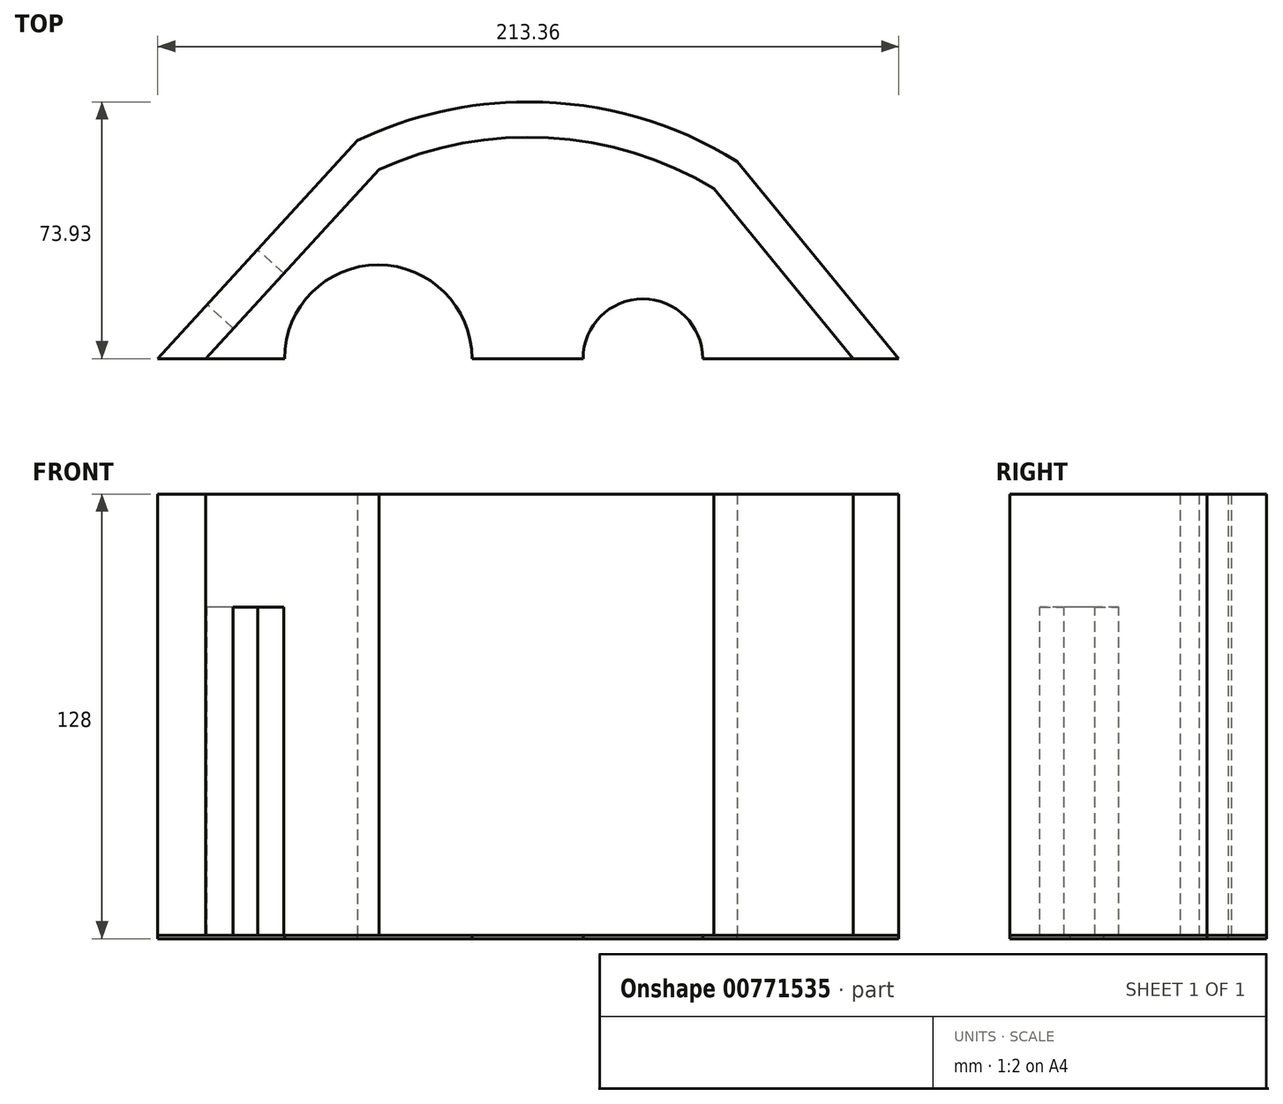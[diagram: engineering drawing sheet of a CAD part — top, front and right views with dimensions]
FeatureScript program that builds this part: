
annotation { "Feature Type Name" : "Feature", "Feature Type Description" : "" }
export const myFeature = defineFeature(function(context is Context, id is Id, definition is map)
    precondition{}
    {
        {
            var Q0;
            Q0=qCreatedBy(makeId("Top.planeOp"),FACE);
            var sketch = newSketch(context, id + "F0", { "sketchPlane" : qUnion([Q0])});
            skLineSegment(sketch, "E0", {"start": v(-47.84, 26.82) * mm, "end": v(37.98, 120.44) * mm});
            skLineSegment(sketch, "E1", {"start": v(37.98, 120.44) * mm, "end": v(88.78, 120.44) * mm});
            skLineSegment(sketch, "E2", {"start": v(-47.84, 26.82) * mm, "end": v(-4.14, 26.82) * mm});
            skLineSegment(sketch, "E3", {"start": v(165.52, 26.82) * mm, "end": v(88.78, 120.44) * mm});
            skLineSegment(sketch, "E4", {"start": v(165.52, 26.82) * mm, "end": v(109.06, 26.82) * mm});
            skCircle(sketch, "E5", {"center": v(15.66, 26.82) * mm, "radius": 12.7 * mm});
            skCircle(sketch, "E6", {"center": v(91.86, 26.82) * mm, "radius": 12.7 * mm});
            skLineSegment(sketch, "E7", {"start": v(154.48, 40.3) * mm, "end": v(122.28, 79.58) * mm});
            skArc(sketch, "E8", {"start": v(109.06, 26.82) * mm, "mid": v(91.86, 44.02) * mm, "end": v(74.66, 26.82) * mm});
            skArc(sketch, "E9", {"start": v(35.46, 26.82) * mm, "mid": v(15.66, 46.62) * mm, "end": v(-4.14, 26.82) * mm});
            skLineSegment(sketch, "E10.trimOffspring", {"start": v(35.46, 26.82) * mm, "end": v(74.66, 26.82) * mm});
            skLineSegment(sketch, "E11.trimOffspring", {"start": v(109.06, 26.82) * mm, "end": v(165.52, 26.82) * mm});
            skSolve(sketch);
        }
        {
            var Q0;
            Q0 = qSketchRegion(id + "F0", true);
            extrude(context, id + "F1", {"entities" : qUnion([Q0]), "depth" : 1 * mm, "offsetDistance" : 25.4 * mm});
        }
        {
            var Q0;
            Q0=makeQuery(id+"F1.opExtrude","SWEPT_BODY",BODY,{"disambiguationData":[OSD([sQuery(id+"F0.wireOp",EDGE,"E6")])]});
            deleteBodies(context, id + "F2", {"entities" : qUnion([Q0])});
        }
        {
            var Q0;
            Q0=makeQuery(id+"F1.opExtrude","SWEPT_BODY",BODY,{"disambiguationData":[OSD([sQuery(id+"F0.wireOp",EDGE,"E5")])]});
            deleteBodies(context, id + "F3", {"entities" : qUnion([Q0])});
        }
        {
            var Q0;
            Q0=makeQuery(id+"F1.opExtrude","CAP_FACE",FACE,{"disambiguationData":[OSD([sQuery(id+"F0.wireOp",EDGE,"E0"),sQuery(id+"F0.wireOp",EDGE,"E1"),sQuery(id+"F0.wireOp",EDGE,"E3"),sQuery(id+"F0.wireOp",EDGE,"E2"),sQuery(id+"F0.wireOp",EDGE,"E7"),sQuery(id+"F0.wireOp",EDGE,"E8"),sQuery(id+"F0.wireOp",EDGE,"E9"),sQuery(id+"F0.wireOp",EDGE,"E10.trimOffspring"),sQuery(id+"F0.wireOp",EDGE,"E11.trimOffspring")])],"isStart":false});
            var sketch = newSketch(context, id + "F4", { "sketchPlane" : qUnion([Q0])});
            skLineSegment(sketch, "E12", {"start": v(-32.88, 96.1) * mm, "end": v(188.48, 96.1) * mm});
            skLineSegment(sketch, "E13", {"start": v(188.48, 96.1) * mm, "end": v(188.48, 149.6) * mm});
            skLineSegment(sketch, "E14", {"start": v(188.48, 149.6) * mm, "end": v(-32.88, 149.6) * mm});
            skLineSegment(sketch, "E15", {"start": v(-32.88, 96.1) * mm, "end": v(-32.88, 149.6) * mm});
            skSolve(sketch);
        }
        {
            var Q0;
            {var subQ4=sQuery(id+"F4.wireOp",EDGE,"E13");Q0=makeQuery(id+"F4.imprint","IMPRINT",FACE,{"disambiguationData":[TD([[makeQuery(id+"F4.imprint","IMPRINT",EDGE,{"derivedFrom":subQ4}),1.0]])]});}
            extrude(context, id + "F5", {"entities" : qUnion([Q0]), "operationType" : NewBodyOperationType.REMOVE, "oppositeDirection" : true, "depth" : 25.4 * mm, "offsetDistance" : 25.4 * mm});
        }
        {
            var Q0;
            Q0=makeQuery(id+"F1.opExtrude","CAP_FACE",FACE,{"disambiguationData":[OSD([sQuery(id+"F0.wireOp",EDGE,"E0"),sQuery(id+"F0.wireOp",EDGE,"E1"),sQuery(id+"F0.wireOp",EDGE,"E3"),sQuery(id+"F0.wireOp",EDGE,"E2"),sQuery(id+"F0.wireOp",EDGE,"E7"),sQuery(id+"F0.wireOp",EDGE,"E8"),sQuery(id+"F0.wireOp",EDGE,"E9"),sQuery(id+"F0.wireOp",EDGE,"E10.trimOffspring"),sQuery(id+"F0.wireOp",EDGE,"E11.trimOffspring")])],"isStart":false});
            var sketch = newSketch(context, id + "F6", { "sketchPlane" : qUnion([Q0])});
            skLineSegment(sketch, "E16", {"start": v(-24.14, 100.75) * mm, "end": v(192.58, 100.75) * mm});
            skLineSegment(sketch, "E17", {"start": v(192.58, 100.75) * mm, "end": v(184.87, 143.2) * mm});
            skLineSegment(sketch, "E18", {"start": v(184.87, 143.2) * mm, "end": v(-26.68, 149.4) * mm});
            skLineSegment(sketch, "E19", {"start": v(-26.68, 149.4) * mm, "end": v(-24.14, 100.75) * mm});
            skSolve(sketch);
        }
        {
            var Q0;
            Q0 = qSketchRegion(id + "F6", true);
            extrude(context, id + "F7", {"entities" : qUnion([Q0]), "operationType" : NewBodyOperationType.REMOVE, "oppositeDirection" : true, "depth" : 25.4 * mm, "offsetDistance" : 25.4 * mm});
        }
        {
            var Q0;
            Q0=makeQuery(id+"F1.opExtrude","CAP_FACE",FACE,{"disambiguationData":[OSD([sQuery(id+"F0.wireOp",EDGE,"E0"),sQuery(id+"F0.wireOp",EDGE,"E1"),sQuery(id+"F0.wireOp",EDGE,"E3"),sQuery(id+"F0.wireOp",EDGE,"E2"),sQuery(id+"F0.wireOp",EDGE,"E7"),sQuery(id+"F0.wireOp",EDGE,"E8"),sQuery(id+"F0.wireOp",EDGE,"E9"),sQuery(id+"F0.wireOp",EDGE,"E10.trimOffspring"),sQuery(id+"F0.wireOp",EDGE,"E11.trimOffspring")])],"isStart":false});
            var sketch = newSketch(context, id + "F8", { "sketchPlane" : qUnion([Q0])});
            skCircle(sketch, "E20", {"center": v(58.84, -13.19) * mm, "radius": 113.94 * mm});
            skPoint(sketch, "E20.first.point", {"position": v(-47.84, 26.82) * mm});
            skPoint(sketch, "E20.second.point", {"position": v(165.52, 26.82) * mm});
            skPoint(sketch, "E20.third.point", {"position": v(58.65, 100.75) * mm});
            skSolve(sketch);
        }
        {
            var Q0;
            {var subQ0=makeQuery(id+"F1.opExtrude","CAP_EDGE",EDGE,{"disambiguationData":[OSD([sQuery(id+"F0.wireOp",EDGE,"E2")])],"isStart":false});Q0=makeQuery(id+"F8.imprint","IMPRINT",FACE,{"disambiguationData":[TD([[makeQuery(id+"F8.imprint","IMPRINT",EDGE,{"derivedFrom":subQ0}),-1.0]])]});}
            var Q1;
            {var subQ0=sQuery(id+"F8.wireOp",EDGE,"E20");var subQ1=makeQuery(id+"F1.opExtrude","CAP_EDGE",EDGE,{"disambiguationData":[OSD([sQuery(id+"F0.wireOp",EDGE,"E3"),sQuery(id+"F0.wireOp",EDGE,"E7")])],"isStart":false});var subQ3=makeQuery(id+"F8.imprint","INTERSECT",VERTEX,{"derivedFrom":[subQ1,subQ0]});Q1=makeQuery(id+"F8.imprint","IMPRINT",FACE,{"disambiguationData":[TD([[makeQuery(id+"F8.imprint","IMPRINT",EDGE,{"disambiguationData":[TD([[subQ3,1.0]])],"derivedFrom":subQ0}),1.0]])]});}
            var Q2;
            {var subQ0=sQuery(id+"F8.wireOp",EDGE,"E20");var subQ1=makeQuery(id+"F7.boolean.opBoolean","COPY",EDGE,{"derivedFrom":makeQuery(id+"F7.opExtrude","CAP_EDGE",EDGE,{"disambiguationData":[OSD([sQuery(id+"F6.wireOp",EDGE,"E16")])],"isStart":true})});var subQ2=makeQuery(id+"F8.imprint","INTERSECT",VERTEX,{"disambiguationData":[OD(0.0)],"derivedFrom":[subQ1,subQ0]});Q2=makeQuery(id+"F8.imprint","IMPRINT",FACE,{"disambiguationData":[TD([[makeQuery(id+"F8.imprint","IMPRINT",EDGE,{"disambiguationData":[TD([[subQ2,-1.0]])],"derivedFrom":subQ0}),1.0]])]});}
            var Q3;
            {var subQ0=sQuery(id+"F8.wireOp",EDGE,"E20");var subQ1=makeQuery(id+"F1.opExtrude","CAP_EDGE",EDGE,{"disambiguationData":[OSD([sQuery(id+"F0.wireOp",EDGE,"E0")])],"isStart":false});var subQ3=makeQuery(id+"F8.imprint","INTERSECT",VERTEX,{"derivedFrom":[subQ1,subQ0]});Q3=makeQuery(id+"F8.imprint","IMPRINT",FACE,{"disambiguationData":[TD([[makeQuery(id+"F8.imprint","IMPRINT",EDGE,{"disambiguationData":[TD([[subQ3,-1.0]])],"derivedFrom":subQ0}),1.0]])]});}
            var Q4;
            {var subQ0=sQuery(id+"F8.wireOp",EDGE,"E20");var subQ1=makeQuery(id+"F7.boolean.opBoolean","COPY",EDGE,{"derivedFrom":makeQuery(id+"F7.opExtrude","CAP_EDGE",EDGE,{"disambiguationData":[OSD([sQuery(id+"F6.wireOp",EDGE,"E16")])],"isStart":true})});var subQ2=makeQuery(id+"F8.imprint","INTERSECT",VERTEX,{"disambiguationData":[OD(1.0)],"derivedFrom":[subQ1,subQ0]});Q4=makeQuery(id+"F8.imprint","IMPRINT",FACE,{"disambiguationData":[TD([[makeQuery(id+"F8.imprint","IMPRINT",EDGE,{"disambiguationData":[TD([[subQ2,-1.0]])],"derivedFrom":subQ0}),-1.0]])]});}
            var Q5;
            {var subQ0=sQuery(id+"F8.wireOp",EDGE,"E20");var subQ3=makeQuery(id+"F7.boolean.opBoolean","COPY",EDGE,{"derivedFrom":makeQuery(id+"F7.opExtrude","CAP_EDGE",EDGE,{"disambiguationData":[OSD([sQuery(id+"F6.wireOp",EDGE,"E16")])],"isStart":true})});var subQ4=makeQuery(id+"F8.imprint","INTERSECT",VERTEX,{"disambiguationData":[OD(0.0)],"derivedFrom":[subQ3,subQ0]});Q5=makeQuery(id+"F8.imprint","IMPRINT",FACE,{"disambiguationData":[TD([[makeQuery(id+"F8.imprint","IMPRINT",EDGE,{"disambiguationData":[TD([[subQ4,1.0]])],"derivedFrom":subQ0}),-1.0]])]});}
            extrude(context, id + "F9", {"entities" : qUnion([Q0, Q1, Q2, Q3, Q4, Q5]), "operationType" : NewBodyOperationType.REMOVE, "oppositeDirection" : true, "depth" : 25.4 * mm, "offsetDistance" : 25.4 * mm});
        }
        {
            var Q0;
            Q0=makeQuery(id+"F1.opExtrude","CAP_FACE",FACE,{"disambiguationData":[OSD([sQuery(id+"F0.wireOp",EDGE,"E0"),sQuery(id+"F0.wireOp",EDGE,"E1"),sQuery(id+"F0.wireOp",EDGE,"E3"),sQuery(id+"F0.wireOp",EDGE,"E2"),sQuery(id+"F0.wireOp",EDGE,"E7"),sQuery(id+"F0.wireOp",EDGE,"E8"),sQuery(id+"F0.wireOp",EDGE,"E9"),sQuery(id+"F0.wireOp",EDGE,"E10.trimOffspring"),sQuery(id+"F0.wireOp",EDGE,"E11.trimOffspring")])],"isStart":false});
            var sketch = newSketch(context, id + "F10", { "sketchPlane" : qUnion([Q0])});
            skCircle(sketch, "E21", {"center": v(15.66, 26.82) * mm, "radius": 27 * mm});
            skSolve(sketch);
        }
        {
            var Q0;
            {var subQ5=makeQuery(id+"F1.opExtrude","CAP_EDGE",EDGE,{"disambiguationData":[OSD([sQuery(id+"F0.wireOp",EDGE,"E9")])],"isStart":false});Q0=makeQuery(id+"F10.imprint","IMPRINT",FACE,{"disambiguationData":[TD([[makeQuery(id+"F10.imprint","IMPRINT",EDGE,{"derivedFrom":subQ5}),-1.0]])]});}
            extrude(context, id + "F11", {"entities" : qUnion([Q0]), "operationType" : NewBodyOperationType.REMOVE, "oppositeDirection" : true, "depth" : 25.4 * mm, "offsetDistance" : 25.4 * mm});
        }
        {
            var Q0;
            Q0=makeQuery(id+"F1.opExtrude","CAP_FACE",FACE,{"disambiguationData":[OSD([sQuery(id+"F0.wireOp",EDGE,"E0"),sQuery(id+"F0.wireOp",EDGE,"E1"),sQuery(id+"F0.wireOp",EDGE,"E3"),sQuery(id+"F0.wireOp",EDGE,"E2"),sQuery(id+"F0.wireOp",EDGE,"E7"),sQuery(id+"F0.wireOp",EDGE,"E8"),sQuery(id+"F0.wireOp",EDGE,"E9"),sQuery(id+"F0.wireOp",EDGE,"E10.trimOffspring"),sQuery(id+"F0.wireOp",EDGE,"E11.trimOffspring")])],"isStart":false});
            var sketch = newSketch(context, id + "F12", { "sketchPlane" : qUnion([Q0])});
            skArc(sketch, "E22", {"start": v(119, 83.57) * mm, "mid": v(65.14, 100.58) * mm, "end": v(9.72, 89.62) * mm});
            skPoint(sketch, "E22.first.point", {"position": v(9.72, 89.62) * mm});
            skPoint(sketch, "E22.second.point", {"position": v(119, 83.57) * mm});
            skPoint(sketch, "E22.third.point", {"position": v(58.65, 100.75) * mm});
            skLineSegment(sketch, "E23", {"start": v(-47.84, 26.82) * mm, "end": v(9.72, 89.62) * mm});
            skLineSegment(sketch, "E24", {"start": v(165.52, 26.82) * mm, "end": v(119, 83.57) * mm});
            skLineSegment(sketch, "E25.0", {"start": v(-34.06, 26.82) * mm, "end": v(15.85, 81.27) * mm});
            skArc(sketch, "E25.1", {"start": v(112.23, 75.8) * mm, "mid": v(64.72, 90.42) * mm, "end": v(15.85, 81.27) * mm});
            skLineSegment(sketch, "E25.2", {"start": v(152.38, 26.82) * mm, "end": v(112.23, 75.8) * mm});
            skLineSegment(sketch, "E26", {"start": v(-47.84, 26.82) * mm, "end": v(-34.06, 26.82) * mm});
            skLineSegment(sketch, "E27", {"start": v(165.52, 26.82) * mm, "end": v(152.38, 26.82) * mm});
            skPoint(sketch, "E28.orphan", {"position": v(-29.59, 26.82) * mm});
            skSolve(sketch);
        }
        {
            var Q0;
            {var subQ1=sQuery(id+"F12.wireOp",EDGE,"E23");Q0=makeQuery(id+"F12.imprint","IMPRINT",FACE,{"disambiguationData":[TD([[makeQuery(id+"F12.imprint","IMPRINT",EDGE,{"derivedFrom":subQ1}),-1.0]])]});}
            extrude(context, id + "F13", {"entities" : qUnion([Q0]), "depth" : 127 * mm, "offsetDistance" : 25.4 * mm});
        }
        {
            var Q0;
            Q0=makeQuery(id+"F13.opExtrude","SWEPT_FACE",FACE,{"disambiguationData":[OSD([sQuery(id+"F12.wireOp",EDGE,"E23")])]});
            var sketch = newSketch(context, id + "F14", { "sketchPlane" : qUnion([Q0])});
            skLineSegment(sketch, "E29.bottom", {"start": v(-30.04, 1) * mm, "end": v(-8.53, 1) * mm});
            skLineSegment(sketch, "E29.top", {"start": v(-30.04, 95.43) * mm, "end": v(-8.53, 95.43) * mm});
            skLineSegment(sketch, "E29.left", {"start": v(-30.04, 1) * mm, "end": v(-30.04, 95.43) * mm});
            skLineSegment(sketch, "E29.right", {"start": v(-8.53, 1) * mm, "end": v(-8.53, 95.43) * mm});
            skSolve(sketch);
        }
        {
            var Q0;
            Q0 = qSketchRegion(id + "F14", true);
            extrude(context, id + "F15", {"entities" : qUnion([Q0]), "operationType" : NewBodyOperationType.REMOVE, "oppositeDirection" : true, "depth" : 25.4 * mm, "offsetDistance" : 25.4 * mm});
        }
    });
